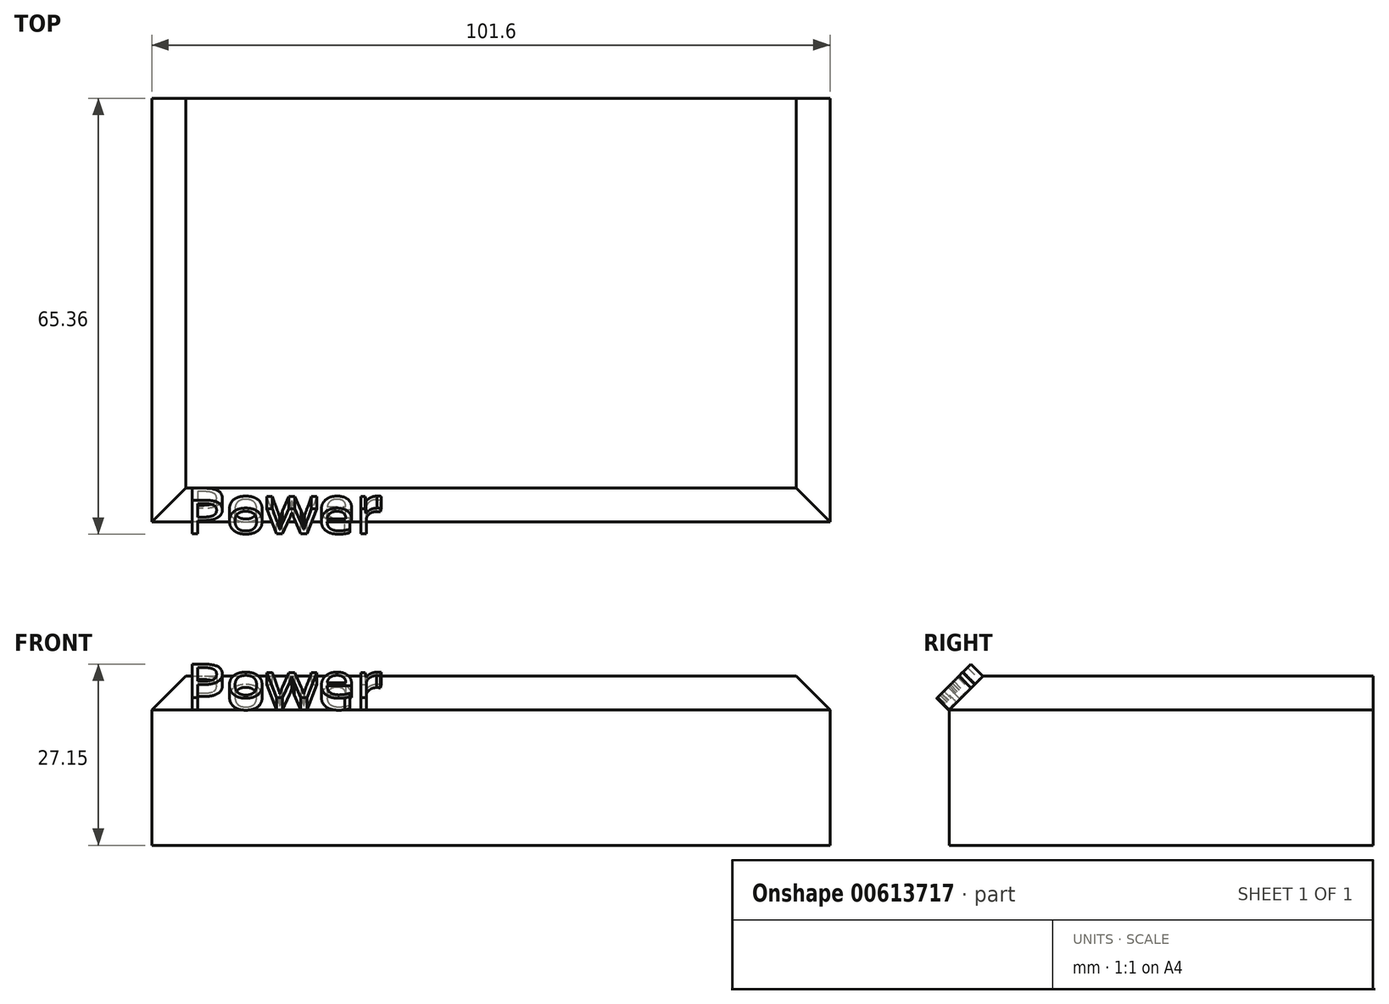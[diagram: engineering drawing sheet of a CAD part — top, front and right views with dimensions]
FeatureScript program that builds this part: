
annotation { "Feature Type Name" : "Feature", "Feature Type Description" : "" }
export const myFeature = defineFeature(function(context is Context, id is Id, definition is map)
    precondition{}
    {
        {
            var Q0;
            Q0=qCreatedBy(makeId("Top.planeOp"),FACE);
            var sketch = newSketch(context, id + "F0", { "sketchPlane" : qUnion([Q0])});
            skLineSegment(sketch, "E0.bottom", {"start": v(-50.8, 31.75) * mm, "end": v(50.8, 31.75) * mm});
            skLineSegment(sketch, "E0.top", {"start": v(-50.8, -31.75) * mm, "end": v(50.8, -31.75) * mm});
            skLineSegment(sketch, "E0.left", {"start": v(-50.8, 31.75) * mm, "end": v(-50.8, -31.75) * mm});
            skLineSegment(sketch, "E0.right", {"start": v(50.8, 31.75) * mm, "end": v(50.8, -31.75) * mm});
            skSolve(sketch);
        }
        {
            var Q0;
            Q0 = qSketchRegion(id + "F0", true);
            extrude(context, id + "F1", {"entities" : qUnion([Q0]), "depth" : 25.4 * mm, "offsetDistance" : 25.4 * mm});
        }
        {
            var Q0;
            Q0=makeQuery(id+"F1.opExtrude","CAP_EDGE",EDGE,{"disambiguationData":[OSD([sQuery(id+"F0.wireOp",EDGE,"E0.right")])],"isStart":false});
            var Q1;
            Q1=makeQuery(id+"F1.opExtrude","CAP_EDGE",EDGE,{"disambiguationData":[OSD([sQuery(id+"F0.wireOp",EDGE,"E0.left")])],"isStart":false});
            var Q2;
            Q2=makeQuery(id+"F1.opExtrude","CAP_EDGE",EDGE,{"disambiguationData":[OSD([sQuery(id+"F0.wireOp",EDGE,"E0.top")])],"isStart":false});
            chamfer(context, id + "F2", {"entities" : qUnion([Q0, Q1, Q2]), "width" : 5.08 * mm, "tangentPropagation" : true});
        }
        {
            var Q0;
            Q0=makeQuery(id+"F2.opChamfer","BLEND_FACE",FACE,{"disambiguationData":[OSD([sQuery(id+"F0.wireOp",EDGE,"E0.top")])]});
            var sketch = newSketch(context, id + "F3", { "sketchPlane" : qUnion([Q0])});
            skText(sketch, "E1", { "text": "Power", "fontName": "OpenSans-Regular.ttf"});
            const initialGuessF3  = {"E1": [-0.04572, -0.00808, 1, 0, 0.00718]};
            skSetInitialGuess(sketch, initialGuessF3);
            skSolve(sketch);
        }
        {
            var Q0;
            Q0 = qSketchRegion(id + "F3", true);
            extrude(context, id + "F4", {"entities" : qUnion([Q0]), "operationType" : NewBodyOperationType.ADD, "depth" : 2.54 * mm, "offsetDistance" : 25.4 * mm});
        }
    });
